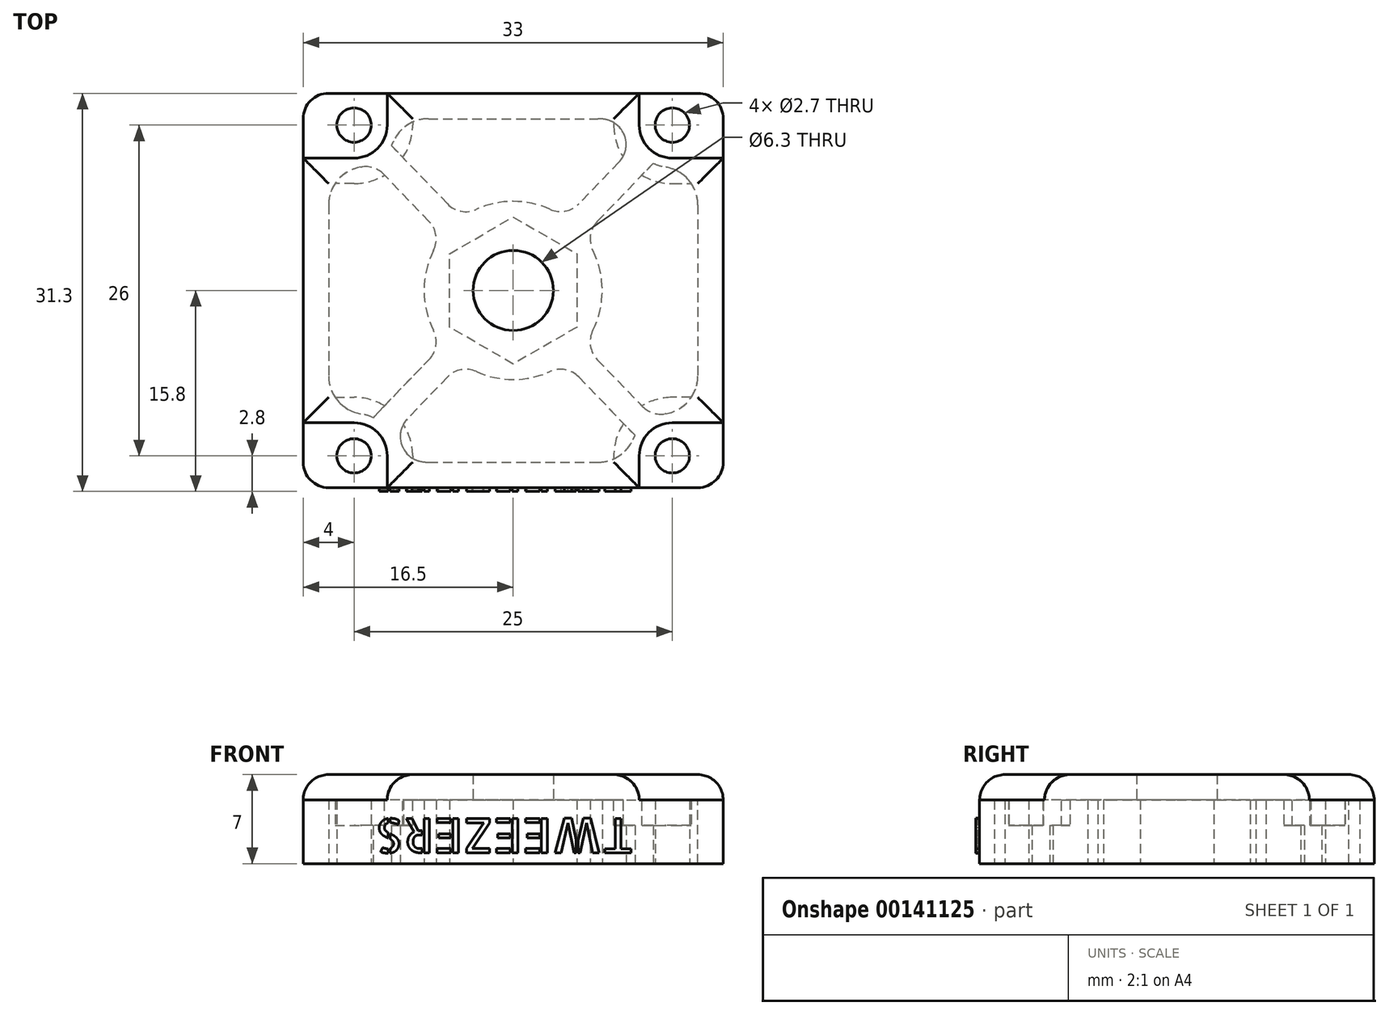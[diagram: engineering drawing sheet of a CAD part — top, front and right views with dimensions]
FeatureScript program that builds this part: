
annotation { "Feature Type Name" : "Feature", "Feature Type Description" : "" }
export const myFeature = defineFeature(function(context is Context, id is Id, definition is map)
    precondition{}
    {
        {
            var Q0;
            Q0=qCreatedBy(makeId("Top.planeOp"),FACE);
            var sketch = newSketch(context, id + "F0", { "sketchPlane" : qUnion([Q0])});
            skPoint(sketch, "E0", {"position": v(-12.5, 13) * mm});
            skPoint(sketch, "E1", {"position": v(12.5, 13) * mm});
            skPoint(sketch, "E2", {"position": v(-12.5, -13) * mm});
            skPoint(sketch, "E3", {"position": v(12.5, -13) * mm});
            skLineSegment(sketch, "E4", {"start": v(0, 33.85) * mm, "end": v(0, -36.04) * mm, "construction": true});
            skLineSegment(sketch, "E5", {"start": v(-33.7, 0) * mm, "end": v(36.4, 0) * mm, "construction": true});
            skLineSegment(sketch, "E6.bottom", {"start": v(-16.5, 15.5) * mm, "end": v(16.5, 15.5) * mm});
            skLineSegment(sketch, "E6.top", {"start": v(-16.5, -15.5) * mm, "end": v(16.5, -15.5) * mm});
            skLineSegment(sketch, "E6.left", {"start": v(-16.5, 15.5) * mm, "end": v(-16.5, -15.5) * mm});
            skLineSegment(sketch, "E6.right", {"start": v(16.5, 15.5) * mm, "end": v(16.5, -15.5) * mm});
            skCircle(sketch, "E7", {"center": v(-12.5, 13) * mm, "radius": 1.35 * mm});
            skCircle(sketch, "E8", {"center": v(12.5, 13) * mm, "radius": 1.35 * mm});
            skCircle(sketch, "E9", {"center": v(-12.5, -13) * mm, "radius": 1.35 * mm});
            skCircle(sketch, "E10", {"center": v(12.5, -13) * mm, "radius": 1.35 * mm});
            skSolve(sketch);
        }
        {
            var Q0;
            Q0=makeQuery(id+"F0.imprint","IMPRINT",FACE,{"disambiguationData":[TD([[makeQuery(id+"F0.imprint","IMPRINT",EDGE,{"derivedFrom":sQuery(id+"F0.wireOp",EDGE,"E6.bottom")}),-1.0]])]});
            extrude(context, id + "F1", {"entities" : qUnion([Q0]), "depth" : 7 * mm});
        }
        {
            var Q0;
            Q0=makeQuery(id+"F1.opExtrude","CAP_FACE",FACE,{"disambiguationData":[OSD([sQuery(id+"F0.wireOp",EDGE,"E6.bottom"),sQuery(id+"F0.wireOp",EDGE,"E6.top"),sQuery(id+"F0.wireOp",EDGE,"E6.left"),sQuery(id+"F0.wireOp",EDGE,"E6.right"),sQuery(id+"F0.wireOp",EDGE,"E7"),sQuery(id+"F0.wireOp",EDGE,"E8"),sQuery(id+"F0.wireOp",EDGE,"E9"),sQuery(id+"F0.wireOp",EDGE,"E10")])],"isStart":false});
            var sketch = newSketch(context, id + "F2", { "sketchPlane" : qUnion([Q0])});
            skLineSegment(sketch, "E11", {"start": v(9.9, 15.5) * mm, "end": v(9.9, 13) * mm});
            skLineSegment(sketch, "E12", {"start": v(12.5, 10.4) * mm, "end": v(16.5, 10.4) * mm});
            skPoint(sketch, "E13.visualSharp", {"position": v(9.9, 10.4) * mm});
            skArc(sketch, "E13.filletArc", {"start": v(9.9, 13) * mm, "mid": v(10.66, 11.16) * mm, "end": v(12.5, 10.4) * mm});
            skLineSegment(sketch, "E14", {"start": v(-9.9, 15.5) * mm, "end": v(-9.9, 13) * mm});
            skLineSegment(sketch, "E15", {"start": v(-12.5, 10.4) * mm, "end": v(-16.5, 10.4) * mm});
            skPoint(sketch, "E16.visualSharp", {"position": v(-9.9, 10.4) * mm});
            skArc(sketch, "E16.filletArc", {"start": v(-12.5, 10.4) * mm, "mid": v(-10.66, 11.16) * mm, "end": v(-9.9, 13) * mm});
            skLineSegment(sketch, "E17", {"start": v(-16.5, -10.4) * mm, "end": v(-12.5, -10.4) * mm});
            skLineSegment(sketch, "E18", {"start": v(-9.9, -13) * mm, "end": v(-9.9, -15.5) * mm});
            skPoint(sketch, "E19.visualSharp", {"position": v(-9.9, -10.4) * mm});
            skArc(sketch, "E19.filletArc", {"start": v(-9.9, -13) * mm, "mid": v(-10.66, -11.16) * mm, "end": v(-12.5, -10.4) * mm});
            skLineSegment(sketch, "E20", {"start": v(16.5, -10.4) * mm, "end": v(12.5, -10.4) * mm});
            skLineSegment(sketch, "E21", {"start": v(9.9, -13) * mm, "end": v(9.9, -15.5) * mm});
            skPoint(sketch, "E22.visualSharp", {"position": v(9.9, -10.4) * mm});
            skArc(sketch, "E22.filletArc", {"start": v(12.5, -10.4) * mm, "mid": v(10.66, -11.16) * mm, "end": v(9.9, -13) * mm});
            skSolve(sketch);
        }
        {
            var Q0;
            Q0=makeQuery(id+"F2.imprint","IMPRINT",FACE,{"disambiguationData":[TD([[makeQuery(id+"F2.imprint","IMPRINT",EDGE,{"derivedFrom":makeQuery(id+"F1.opExtrude","CAP_EDGE",EDGE,{"disambiguationData":[OSD([sQuery(id+"F0.wireOp",EDGE,"E7")])],"isStart":false})}),-1.0]])]});
            var Q1;
            Q1=makeQuery(id+"F2.imprint","IMPRINT",FACE,{"disambiguationData":[TD([[makeQuery(id+"F2.imprint","IMPRINT",EDGE,{"derivedFrom":makeQuery(id+"F1.opExtrude","CAP_EDGE",EDGE,{"disambiguationData":[OSD([sQuery(id+"F0.wireOp",EDGE,"E8")])],"isStart":false})}),-1.0]])]});
            var Q2;
            {var subQ4=sQuery(id+"F2.wireOp",EDGE,"E17");Q2=makeQuery(id+"F2.imprint","IMPRINT",FACE,{"disambiguationData":[TD([[makeQuery(id+"F2.imprint","IMPRINT",EDGE,{"derivedFrom":subQ4}),-1.0]])]});}
            var Q3;
            {var subQ1=sQuery(id+"F2.wireOp",EDGE,"E20");Q3=makeQuery(id+"F2.imprint","IMPRINT",FACE,{"disambiguationData":[TD([[makeQuery(id+"F2.imprint","IMPRINT",EDGE,{"derivedFrom":subQ1}),1.0]])]});}
            extrude(context, id + "F3", {"entities" : qUnion([Q0, Q1, Q2, Q3]), "operationType" : NewBodyOperationType.REMOVE, "oppositeDirection" : true, "depth" : 2 * mm});
        }
        {
            var Q0;
            Q0=makeQuery(id+"F1.opExtrude","CAP_FACE",FACE,{"disambiguationData":[OSD([sQuery(id+"F0.wireOp",EDGE,"E6.bottom"),sQuery(id+"F0.wireOp",EDGE,"E6.top"),sQuery(id+"F0.wireOp",EDGE,"E6.left"),sQuery(id+"F0.wireOp",EDGE,"E6.right"),sQuery(id+"F0.wireOp",EDGE,"E7"),sQuery(id+"F0.wireOp",EDGE,"E8"),sQuery(id+"F0.wireOp",EDGE,"E9"),sQuery(id+"F0.wireOp",EDGE,"E10")])],"isStart":true});
            shell(context, id + "F4", {"entities" : qUnion([Q0]), "thickness" : 2 * mm});
        }
        {
            var Q0;
            Q0=makeQuery(id+"F1.opExtrude","CAP_FACE",FACE,{"disambiguationData":[OSD([sQuery(id+"F0.wireOp",EDGE,"E6.bottom"),sQuery(id+"F0.wireOp",EDGE,"E6.top"),sQuery(id+"F0.wireOp",EDGE,"E6.left"),sQuery(id+"F0.wireOp",EDGE,"E6.right"),sQuery(id+"F0.wireOp",EDGE,"E7"),sQuery(id+"F0.wireOp",EDGE,"E8"),sQuery(id+"F0.wireOp",EDGE,"E9"),sQuery(id+"F0.wireOp",EDGE,"E10")])],"isStart":false});
            var Q1;
            Q1=makeQuery(id+"F3.boolean.opBoolean","COPY",EDGE,{"derivedFrom":makeQuery(id+"F3.opExtrude","SWEPT_EDGE",EDGE,{"disambiguationData":[OSD([sQuery(id+"F0.wireOp",EDGE,"E6.top"),sQuery(id+"F2.wireOp",EDGE,"E18")])]})});
            var Q2;
            Q2=makeQuery(id+"F3.boolean.opBoolean","COPY",EDGE,{"derivedFrom":makeQuery(id+"F3.opExtrude","SWEPT_EDGE",EDGE,{"disambiguationData":[OSD([sQuery(id+"F0.wireOp",EDGE,"E6.left"),sQuery(id+"F2.wireOp",EDGE,"E17")])]})});
            var Q3;
            Q3=makeQuery(id+"F1.opExtrude","SWEPT_EDGE",EDGE,{"disambiguationData":[OSD([sQuery(id+"F0.wireOp",EDGE,"E6.bottom"),sQuery(id+"F0.wireOp",EDGE,"E6.right")])]});
            var Q4;
            Q4=makeQuery(id+"F3.boolean.opBoolean","COPY",EDGE,{"derivedFrom":makeQuery(id+"F3.opExtrude","SWEPT_EDGE",EDGE,{"disambiguationData":[OSD([sQuery(id+"F0.wireOp",EDGE,"E6.bottom"),sQuery(id+"F2.wireOp",EDGE,"E11")])]})});
            var Q5;
            Q5=makeQuery(id+"F3.boolean.opBoolean","COPY",EDGE,{"derivedFrom":makeQuery(id+"F3.opExtrude","SWEPT_EDGE",EDGE,{"disambiguationData":[OSD([sQuery(id+"F0.wireOp",EDGE,"E6.right"),sQuery(id+"F2.wireOp",EDGE,"E12")])]})});
            var Q6;
            Q6=makeQuery(id+"F3.boolean.opBoolean","COPY",EDGE,{"derivedFrom":makeQuery(id+"F3.opExtrude","SWEPT_EDGE",EDGE,{"disambiguationData":[OSD([sQuery(id+"F0.wireOp",EDGE,"E6.right"),sQuery(id+"F2.wireOp",EDGE,"E20")])]})});
            var Q7;
            Q7=makeQuery(id+"F1.opExtrude","SWEPT_EDGE",EDGE,{"disambiguationData":[OSD([sQuery(id+"F0.wireOp",EDGE,"E6.top"),sQuery(id+"F0.wireOp",EDGE,"E6.right")])]});
            var Q8;
            Q8=makeQuery(id+"F3.boolean.opBoolean","COPY",EDGE,{"derivedFrom":makeQuery(id+"F3.opExtrude","SWEPT_EDGE",EDGE,{"disambiguationData":[OSD([sQuery(id+"F0.wireOp",EDGE,"E6.top"),sQuery(id+"F2.wireOp",EDGE,"E21")])]})});
            var Q9;
            Q9=makeQuery(id+"F1.opExtrude","SWEPT_EDGE",EDGE,{"disambiguationData":[OSD([sQuery(id+"F0.wireOp",EDGE,"E6.top"),sQuery(id+"F0.wireOp",EDGE,"E6.left")])]});
            var Q10;
            Q10=makeQuery(id+"F3.boolean.opBoolean","COPY",EDGE,{"derivedFrom":makeQuery(id+"F3.opExtrude","SWEPT_EDGE",EDGE,{"disambiguationData":[OSD([sQuery(id+"F0.wireOp",EDGE,"E6.left"),sQuery(id+"F2.wireOp",EDGE,"E15")])]})});
            var Q11;
            Q11=makeQuery(id+"F3.boolean.opBoolean","COPY",EDGE,{"derivedFrom":makeQuery(id+"F3.opExtrude","SWEPT_EDGE",EDGE,{"disambiguationData":[OSD([sQuery(id+"F0.wireOp",EDGE,"E6.bottom"),sQuery(id+"F2.wireOp",EDGE,"E14")])]})});
            var Q12;
            Q12=makeQuery(id+"F1.opExtrude","SWEPT_EDGE",EDGE,{"disambiguationData":[OSD([sQuery(id+"F0.wireOp",EDGE,"E6.bottom"),sQuery(id+"F0.wireOp",EDGE,"E6.left")])]});
            fillet(context, id + "F5", {"entities" : qUnion([Q0, Q1, Q2, Q3, Q4, Q5, Q6, Q7, Q8, Q9, Q10, Q11, Q12]), "radius" : 2 * mm, "tangentPropagation" : true, "allowEdgeOverflow" : false});
        }
        {
            var Q0;
            Q0=qCreatedBy(makeId("Top.planeOp"),FACE);
            var sketch = newSketch(context, id + "F6", { "sketchPlane" : qUnion([Q0])});
            skPoint(sketch, "E23", {"position": v(0, 0) * mm});
            skCircle(sketch, "E24", {"center": v(0, 0) * mm, "radius": 3.15 * mm});
            skCircle(sketch, "E25.cCircle", {"center": v(0, 0) * mm, "radius": 5 * mm, "construction": true});
            skLineSegment(sketch, "E25.0", {"start": v(5, 2.89) * mm, "end": v(5, -2.89) * mm});
            skLineSegment(sketch, "E25.1", {"start": v(5, -2.89) * mm, "end": v(0, -5.77) * mm});
            skLineSegment(sketch, "E25.2", {"start": v(0, -5.77) * mm, "end": v(-5, -2.89) * mm});
            skLineSegment(sketch, "E25.3", {"start": v(-5, -2.89) * mm, "end": v(-5, 2.89) * mm});
            skLineSegment(sketch, "E25.4", {"start": v(-5, 2.89) * mm, "end": v(0, 5.77) * mm});
            skLineSegment(sketch, "E25.5", {"start": v(0, 5.77) * mm, "end": v(5, 2.89) * mm});
            skPoint(sketch, "E25.0.midPoint", {"position": v(5, 0) * mm});
            skCircle(sketch, "E26", {"center": v(0, 0) * mm, "radius": 7 * mm});
            skLineSegment(sketch, "E27", {"start": v(-4.08, -5.69) * mm, "end": v(-9.56, -11.39) * mm});
            skLineSegment(sketch, "E28", {"start": v(-11, -10) * mm, "end": v(-5.52, -4.3) * mm});
            skLineSegment(sketch, "E29", {"start": v(-12.5, -13) * mm, "end": v(0, 0) * mm, "construction": true});
            skLineSegment(sketch, "E30", {"start": v(0, 0) * mm, "end": v(12.5, -13) * mm, "construction": true});
            skLineSegment(sketch, "E31", {"start": v(4.08, -5.69) * mm, "end": v(9.56, -11.39) * mm});
            skLineSegment(sketch, "E32", {"start": v(5.52, -4.3) * mm, "end": v(11, -10) * mm});
            skLineSegment(sketch, "E33", {"start": v(-4.08, 5.69) * mm, "end": v(-9.56, 11.39) * mm});
            skLineSegment(sketch, "E34", {"start": v(-5.52, 4.3) * mm, "end": v(-11, 10) * mm});
            skLineSegment(sketch, "E35", {"start": v(0, 0) * mm, "end": v(-12.5, 13) * mm, "construction": true});
            skLineSegment(sketch, "E36", {"start": v(12.5, 13) * mm, "end": v(0, 0) * mm, "construction": true});
            skArc(sketch, "E37.0", {"start": v(9.19, 13.5) * mm, "mid": v(10.78, 10.13) * mm, "end": v(14.5, 10.31) * mm});
            skLineSegment(sketch, "E38", {"start": v(5.52, 4.3) * mm, "end": v(11, 10) * mm});
            skLineSegment(sketch, "E39", {"start": v(9.56, 11.39) * mm, "end": v(4.08, 5.69) * mm});
            skArc(sketch, "E40.0", {"start": v(14.5, -10.31) * mm, "mid": v(10.78, -10.13) * mm, "end": v(9.19, -13.5) * mm});
            skArc(sketch, "E41.0", {"start": v(-9.19, -13.5) * mm, "mid": v(-10.78, -10.13) * mm, "end": v(-14.5, -10.31) * mm});
            skArc(sketch, "E42.0", {"start": v(-14.5, 10.31) * mm, "mid": v(-10.78, 10.13) * mm, "end": v(-9.19, 13.5) * mm});
            skSolve(sketch);
        }
        {
            var Q0;
            {var subQ0=sQuery(id+"F6.wireOp",EDGE,"E38");var subQ1=sQuery(id+"F6.wireOp",EDGE,"E26");var subQ2=makeQuery(id+"F6.imprint","INTERSECT",VERTEX,{"derivedFrom":[subQ1,subQ0]});Q0=makeQuery(id+"F6.imprint","IMPRINT",FACE,{"disambiguationData":[TD([[makeQuery(id+"F6.imprint","IMPRINT",EDGE,{"disambiguationData":[TD([[subQ2,-1.0]])],"derivedFrom":subQ1}),-1.0]])]});}
            var Q1;
            Q1=makeQuery(id+"F6.imprint","IMPRINT",FACE,{"disambiguationData":[TD([[makeQuery(id+"F6.imprint","IMPRINT",EDGE,{"derivedFrom":sQuery(id+"F6.wireOp",EDGE,"E25.0")}),1.0]])]});
            var Q2;
            {var subQ0=sQuery(id+"F6.wireOp",EDGE,"E27");Q2=makeQuery(id+"F6.imprint","IMPRINT",FACE,{"disambiguationData":[TD([[makeQuery(id+"F6.imprint","IMPRINT",EDGE,{"derivedFrom":subQ0}),-1.0]])]});}
            var Q3;
            {var subQ0=sQuery(id+"F6.wireOp",EDGE,"E33");Q3=makeQuery(id+"F6.imprint","IMPRINT",FACE,{"disambiguationData":[TD([[makeQuery(id+"F6.imprint","IMPRINT",EDGE,{"derivedFrom":subQ0}),1.0]])]});}
            var Q4;
            {var subQ0=sQuery(id+"F6.wireOp",EDGE,"E31");Q4=makeQuery(id+"F6.imprint","IMPRINT",FACE,{"disambiguationData":[TD([[makeQuery(id+"F6.imprint","IMPRINT",EDGE,{"derivedFrom":subQ0}),1.0]])]});}
            var Q5;
            Q5=makeQuery(id+"F4.opShell","OFFSET_FACE",FACE,{"disambiguationData":[OSD([sQuery(id+"F0.wireOp",EDGE,"E6.bottom"),sQuery(id+"F0.wireOp",EDGE,"E6.top"),sQuery(id+"F0.wireOp",EDGE,"E6.left"),sQuery(id+"F0.wireOp",EDGE,"E6.right"),sQuery(id+"F0.wireOp",EDGE,"E7"),sQuery(id+"F0.wireOp",EDGE,"E8"),sQuery(id+"F0.wireOp",EDGE,"E9"),sQuery(id+"F0.wireOp",EDGE,"E10")])]});
            extrude(context, id + "F7", {"entities" : qUnion([Q0, Q1, Q2, Q3, Q4]), "operationType" : NewBodyOperationType.ADD, "endBound" : BoundingType.UP_TO_SURFACE, "endBoundEntityFace" : qUnion([Q5]), "depth" : 25 * mm});
        }
        {
            var Q0;
            Q0=makeQuery(id+"F6.imprint","IMPRINT",FACE,{"disambiguationData":[TD([[makeQuery(id+"F6.imprint","IMPRINT",EDGE,{"derivedFrom":sQuery(id+"F6.wireOp",EDGE,"E24")}),1.0]])]});
            extrude(context, id + "F8", {"entities" : qUnion([Q0]), "operationType" : NewBodyOperationType.REMOVE, "endBound" : BoundingType.THROUGH_ALL, "depth" : 25 * mm});
        }
        {
            var Q0;
            Q0=makeQuery(id+"F4.opShell","TWEAK_EDGE",EDGE,{"derivedFrom":[makeQuery(id+"F1.opExtrude","SWEPT_FACE",FACE,{"disambiguationData":[OSD([sQuery(id+"F0.wireOp",EDGE,"E6.right")])]}),makeQuery(id+"F1.opExtrude","SWEPT_FACE",FACE,{"disambiguationData":[OSD([sQuery(id+"F0.wireOp",EDGE,"E10")])]})]});
            var Q1;
            Q1=makeQuery(id+"F4.opShell","TWEAK_EDGE",EDGE,{"derivedFrom":[makeQuery(id+"F1.opExtrude","SWEPT_FACE",FACE,{"disambiguationData":[OSD([sQuery(id+"F0.wireOp",EDGE,"E6.top")])]}),makeQuery(id+"F1.opExtrude","SWEPT_FACE",FACE,{"disambiguationData":[OSD([sQuery(id+"F0.wireOp",EDGE,"E10")])]})]});
            var Q2;
            Q2=makeQuery(id+"F4.opShell","TWEAK_EDGE",EDGE,{"derivedFrom":[makeQuery(id+"F1.opExtrude","SWEPT_FACE",FACE,{"disambiguationData":[OSD([sQuery(id+"F0.wireOp",EDGE,"E6.top")])]}),makeQuery(id+"F1.opExtrude","SWEPT_FACE",FACE,{"disambiguationData":[OSD([sQuery(id+"F0.wireOp",EDGE,"E9")])]})]});
            var Q3;
            Q3=makeQuery(id+"F4.opShell","TWEAK_EDGE",EDGE,{"derivedFrom":[makeQuery(id+"F1.opExtrude","SWEPT_FACE",FACE,{"disambiguationData":[OSD([sQuery(id+"F0.wireOp",EDGE,"E6.left")])]}),makeQuery(id+"F1.opExtrude","SWEPT_FACE",FACE,{"disambiguationData":[OSD([sQuery(id+"F0.wireOp",EDGE,"E9")])]})]});
            var Q4;
            Q4=makeQuery(id+"F4.opShell","TWEAK_EDGE",EDGE,{"derivedFrom":[makeQuery(id+"F1.opExtrude","SWEPT_FACE",FACE,{"disambiguationData":[OSD([sQuery(id+"F0.wireOp",EDGE,"E6.left")])]}),makeQuery(id+"F1.opExtrude","SWEPT_FACE",FACE,{"disambiguationData":[OSD([sQuery(id+"F0.wireOp",EDGE,"E7")])]})]});
            var Q5;
            Q5=makeQuery(id+"F4.opShell","TWEAK_EDGE",EDGE,{"derivedFrom":[makeQuery(id+"F1.opExtrude","SWEPT_FACE",FACE,{"disambiguationData":[OSD([sQuery(id+"F0.wireOp",EDGE,"E6.bottom")])]}),makeQuery(id+"F1.opExtrude","SWEPT_FACE",FACE,{"disambiguationData":[OSD([sQuery(id+"F0.wireOp",EDGE,"E7")])]})]});
            var Q6;
            Q6=makeQuery(id+"F4.opShell","TWEAK_EDGE",EDGE,{"derivedFrom":[makeQuery(id+"F1.opExtrude","SWEPT_FACE",FACE,{"disambiguationData":[OSD([sQuery(id+"F0.wireOp",EDGE,"E6.right")])]}),makeQuery(id+"F1.opExtrude","SWEPT_FACE",FACE,{"disambiguationData":[OSD([sQuery(id+"F0.wireOp",EDGE,"E8")])]})]});
            var Q7;
            Q7=makeQuery(id+"F4.opShell","TWEAK_EDGE",EDGE,{"derivedFrom":[makeQuery(id+"F1.opExtrude","SWEPT_FACE",FACE,{"disambiguationData":[OSD([sQuery(id+"F0.wireOp",EDGE,"E6.bottom")])]}),makeQuery(id+"F1.opExtrude","SWEPT_FACE",FACE,{"disambiguationData":[OSD([sQuery(id+"F0.wireOp",EDGE,"E8")])]})]});
            fillet(context, id + "F9", {"entities" : qUnion([Q0, Q1, Q2, Q3, Q4, Q5, Q6, Q7]), "radius" : 3 * mm, "allowEdgeOverflow" : false});
        }
        {
            var Q0;
            Q0=makeQuery(id+"F1.opExtrude","SWEPT_FACE",FACE,{"disambiguationData":[OSD([sQuery(id+"F0.wireOp",EDGE,"E6.top")])]});
            var sketch = newSketch(context, id + "F10", { "sketchPlane" : qUnion([Q0])});
            skText(sketch, "E43", { "text": "TWEEZERS", "fontName": "AllertaStencil-Regular.ttf"});
            const initialGuessF10  = {"E43": [0.00945, 0.00355, -1, 0, 0.0027]};
            skSetInitialGuess(sketch, initialGuessF10);
            skSolve(sketch);
        }
        {
            var Q0;
            Q0 = qSketchRegion(id + "F10", true);
            extrude(context, id + "F11", {"entities" : qUnion([Q0]), "operationType" : NewBodyOperationType.ADD, "depth" : 0.3 * mm});
        }
        {
            var Q0;
            Q0=makeQuery(id+"F7.opExtrude","SWEPT_EDGE",EDGE,{"disambiguationData":[OSD([sQuery(id+"F6.wireOp",EDGE,"E26"),sQuery(id+"F6.wireOp",EDGE,"E28")])]});
            var Q1;
            Q1=makeQuery(id+"F7.opExtrude","SWEPT_EDGE",EDGE,{"disambiguationData":[OSD([sQuery(id+"F6.wireOp",EDGE,"E26"),sQuery(id+"F6.wireOp",EDGE,"E34")])]});
            var Q2;
            Q2=makeQuery(id+"F7.opExtrude","SWEPT_EDGE",EDGE,{"disambiguationData":[OSD([sQuery(id+"F6.wireOp",EDGE,"E26"),sQuery(id+"F6.wireOp",EDGE,"E33")])]});
            var Q3;
            Q3=makeQuery(id+"F7.opExtrude","SWEPT_EDGE",EDGE,{"disambiguationData":[OSD([sQuery(id+"F6.wireOp",EDGE,"E26"),sQuery(id+"F6.wireOp",EDGE,"E39")])]});
            var Q4;
            Q4=makeQuery(id+"F7.opExtrude","SWEPT_EDGE",EDGE,{"disambiguationData":[OSD([sQuery(id+"F6.wireOp",EDGE,"E26"),sQuery(id+"F6.wireOp",EDGE,"E38")])]});
            var Q5;
            Q5=makeQuery(id+"F7.opExtrude","SWEPT_EDGE",EDGE,{"disambiguationData":[OSD([sQuery(id+"F6.wireOp",EDGE,"E26"),sQuery(id+"F6.wireOp",EDGE,"E32")])]});
            var Q6;
            Q6=makeQuery(id+"F7.opExtrude","SWEPT_EDGE",EDGE,{"disambiguationData":[OSD([sQuery(id+"F6.wireOp",EDGE,"E26"),sQuery(id+"F6.wireOp",EDGE,"E31")])]});
            var Q7;
            Q7=makeQuery(id+"F7.opExtrude","SWEPT_EDGE",EDGE,{"disambiguationData":[OSD([sQuery(id+"F6.wireOp",EDGE,"E26"),sQuery(id+"F6.wireOp",EDGE,"E27")])]});
            var Q8;
            Q8=makeQuery(id+"F7.opExtrude","SWEPT_EDGE",EDGE,{"disambiguationData":[OSD([sQuery(id+"F6.wireOp",EDGE,"E33"),sQuery(id+"F6.wireOp",EDGE,"E42.0")])]});
            var Q9;
            Q9=makeQuery(id+"F7.opExtrude","SWEPT_EDGE",EDGE,{"disambiguationData":[OSD([sQuery(id+"F6.wireOp",EDGE,"E34"),sQuery(id+"F6.wireOp",EDGE,"E42.0")])]});
            var Q10;
            Q10=makeQuery(id+"F7.opExtrude","SWEPT_EDGE",EDGE,{"disambiguationData":[OSD([sQuery(id+"F6.wireOp",EDGE,"E37.0"),sQuery(id+"F6.wireOp",EDGE,"E38")])]});
            var Q11;
            Q11=makeQuery(id+"F7.opExtrude","SWEPT_EDGE",EDGE,{"disambiguationData":[OSD([sQuery(id+"F6.wireOp",EDGE,"E37.0"),sQuery(id+"F6.wireOp",EDGE,"E39")])]});
            var Q12;
            Q12=makeQuery(id+"F7.opExtrude","SWEPT_EDGE",EDGE,{"disambiguationData":[OSD([sQuery(id+"F6.wireOp",EDGE,"E32"),sQuery(id+"F6.wireOp",EDGE,"E40.0")])]});
            var Q13;
            Q13=makeQuery(id+"F7.opExtrude","SWEPT_EDGE",EDGE,{"disambiguationData":[OSD([sQuery(id+"F6.wireOp",EDGE,"E31"),sQuery(id+"F6.wireOp",EDGE,"E40.0")])]});
            var Q14;
            Q14=makeQuery(id+"F7.opExtrude","SWEPT_EDGE",EDGE,{"disambiguationData":[OSD([sQuery(id+"F6.wireOp",EDGE,"E28"),sQuery(id+"F6.wireOp",EDGE,"E41.0")])]});
            var Q15;
            Q15=makeQuery(id+"F7.opExtrude","SWEPT_EDGE",EDGE,{"disambiguationData":[OSD([sQuery(id+"F6.wireOp",EDGE,"E27"),sQuery(id+"F6.wireOp",EDGE,"E41.0")])]});
            fillet(context, id + "F12", {"entities" : qUnion([Q0, Q1, Q2, Q3, Q4, Q5, Q6, Q7, Q8, Q9, Q10, Q11, Q12, Q13, Q14, Q15]), "radius" : 2 * mm, "allowEdgeOverflow" : false});
        }
    });
